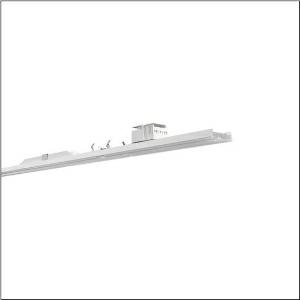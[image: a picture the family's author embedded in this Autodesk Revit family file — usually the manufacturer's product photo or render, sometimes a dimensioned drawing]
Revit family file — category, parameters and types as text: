
# Revit family: licross_r__11_recessed_mo_51tl1ecn48xf_7d4b
name_source: partatom
category: Lighting Fixtures
units: mm (PartAtom-declared; Revit-internal decimal feet)

## family parameters
Cut with Voids When Loaded = No
Host = Face
Light Source = No
Part Type = Normal
Room Calculation Point = No
Round Connector Dimension = Use Diameter
Shared = No

## types (1)
- --- (1 x LED, 8020 lm, 48 W, 4000K)
    Apparent Load = 48 VA
    CIE Flux Codes = 85 95 99 100 100
    Color Rendering = 80
    Color Temperature = 4000K
    Default Elevation = 1800 mm
    Description = Licross® 11 Recessed MO, luminaire insert, of sheet steel, galvanised, coil coated, white, length: 1.500mm, width: 66mm, height: 67mm, LED rated luminous flux: 8.020lm, light colour: 840, control gear: ON/OFF Multilumen, CLOi, control gear: ECG Multilumen, with plug, 3-pole, with phase selection, mains connection: 220..240V, AC, 50/60Hz, halogen-free wiring, primary optical cover: cover, of PMMA, light emission: direct distribution, protection rating (complete): IP40, insulation class (complete): insulation class I (protective earthing), certification: CE, ENEC, VDE, UKCA, protection symbol: D if used in an environment without relevant dust loads with corresponding accessories, permissible ambient temperature for indoor applications: -35..+40°C, reducing of maximum allowable ambient temperature of 5°C with ceiling mounting, corresponds to IFS (International Featured Standards) requirements for safety and quality in the food industry, LABS conformity tested according to VDMA 24364:2018-05, packaging unit: 1 piece
    Height = 58 mm
    Lamp = 1 x LED
    Lamp Light Flux = 8020 lm
    Lamp Power = 48 W
    Lamp count = 1
    Length = 1500 mm
    Luminous efficacy = 167 lm/W
    Manufacturer = Siteco
    ModVariant = No
    Model = 51TL1ECN48XF
    Mounting Place = Ceiling
    Mounting Type = Pendant
    Number of Poles = 1
    OnlyDefault = Yes
    Power Factor = 1
    Product Name = Licross® 11 Recessed MO
    Product group = luminaire insert
    ProductGroupID = 902
    Protection Class = Protection class I
    Protection Degree = IP 40
    RLX_Detail_Level = 1
    RlxData = <blob elided: 20313 chars, md5=126306eb>
    Socket = socket
    Standby Power = 0 W
    System Light Flux = 8020 lm
    System Power = 48 W
    Type Comments = factory setting: luminous flux: 100 % | (A | C | E) | 109 mA
    Type Image = l_1266722.jpg
    URL = http://relux.com
    VarID = @adj_092429
    Voltage = 0 V
    Weight = 0.00 kg
    Width = 66 mm

## geometry (parser evidence)
native form markers: Blend x4, Sweep x11
no freeform markers — native parametric forms only
